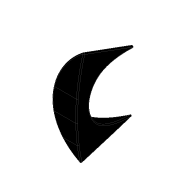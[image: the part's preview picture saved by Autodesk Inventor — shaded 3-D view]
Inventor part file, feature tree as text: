
AUTODESK INVENTOR PART (.ipt)
format: ipt  version: 2020 (Build 240168000, 168)  size: 567,296 bytes
history: native  units: in
note: dims shown in document units (in); Inventor stores cm internally (conversion verified against a paired STEP export)
features: fillet x3, extrude x1, sketch x1
ambient origin geometry x8: Origin, YZ Plane, XZ Plane, XY Plane, X Axis, Y Axis, Z Axis, Center Point
bodies: Solid1 (feature_tree)
feature tree (5):
  extrude  "Extrusion1"  Depth=4.6457in
  fillet  "Fillet1"  Radius=0.0787in
  fillet  "Fillet2"  Radius=0.0787in
  fillet  "Fillet3"  [1 undecoded]
  sketch  "Sketch1"  dims[d0=1.9685in d1=0.0in d2=4.6457in d3=0.0787in d4=0.0787in]
note: 1 required parameter value undecoded (feature->parameter linkage not recoverable at this tier; creation-order binding heuristic only, values carry confidence <= 0.55)
